# Revit family: Screen-NanaWall-Screen_ONE
name_source: partatom
category: Doors
units: mm (PartAtom-declared; Revit-internal decimal feet)

## family parameters
Always vertical = Yes
Classification Number = 23.30.10.24.14
Cut with Voids When Loaded = No
Host = Wall
Room Calculation Point = No
Shared = No

## types (3) — shared parameters
Description = Door Screen
Door System Height = 8' - 0"
Finish = Metal - NanaWall - Aluminum
Function = Interior
Installation and Service URL = http://www.nanawall.com
Keynote = 08 41 00
Manufacturer = NanaWall Systems, Inc.
Manufacturer Fax = (415) 383-0312
Operation = Sliding
Product Name = Screen ONE
Product Page URL = http://www.nanawall.com
Rough Width = 10' - 0"
Size Note = Adjust Height and Width as necessary to fit your project needs. See Product Page URL for more information.
Thickness = 0' - 1 1/2"
URL = http://www.nanawall.com
Wall Closure = By host
Width = 10' - 0"
Width C = 10' - 0"

## per-type parameters (varying)
| type | Height | Height C | L Track | Left | Left Right | Model | R Track | Right | Rough Height | Screen On A Folding Door System | Void Plan L | Void Plan R |
| NS1 Left/ Right | 8' - 1 1/2" | 8' - 1 1/2" | 0' - 3 3/16" | No | Yes | NSLR | 0' - 3 3/16" | No | 8' - 4 1/8" | No | 0' - 3 1/4" | 0' - 3 1/4" |
| NS1 Left | 8' - 2 1/2" | 8' - 2 1/2" | 0' - 3 3/16" | Yes | No | NS1L | 0' - 0 3/4" | No | 8' - 5 1/8" | Yes | 0' - 3 1/4" | 0' - 1 3/8" |
| NS1 Right | 8' - 2 1/2" | 8' - 2 1/2" | 0' - 0 3/4" | No | No | NS1R | 0' - 3 3/16" | Yes | 8' - 5 1/8" | Yes | 0' - 1 3/8" | 0' - 3 1/4" |

## geometry (parser evidence)
native form markers: Blend x4, Sweep x7
no freeform markers — native parametric forms only
